# Revit family: QF_Franke_AC125CL_Foot05_en
name_source: partatom
category: Specialty Equipment
revit_build: Autodesk Revit 2018 (Build: 20170223_1515(x64)
units: mm (PartAtom-declared; Revit-internal decimal feet)

## family parameters
Always vertical = Yes
Cut with Voids When Loaded = No
OmniClass Number = 23.40.40.00
OmniClass Title = Food Service Equipment and Furnishings
Part Type = Normal
Room Calculation Point = No
Round Connector Dimension = Use Diameter
Shared = No
Work Plane-Based = No

## types (1)
- 110-240V 1L N PE data depending on system 10A - (all)
    Assembly Code = E1090320
    CE Approved = Yes
    Conn Conduit = Yes
    Cover front = QF_Black
    Cycle = 0 Hz
    Cycle Alternative = 0 Hz
    Depth Actual = 310 mm  [stored 1.01706 ft]
    ETL Approved = Yes
    Energy efficiency label = -
    Energy loss acc. to DIN 18873 = -
    Height Actual = 155 mm  [stored 0.50853 ft]
    Installed By = Franke technician or authorized Franke partner company
    Keynote = 11 46 23
    Length Actual = 125 mm  [stored 0.410105 ft]
    Manufacturer = Franke Kaffeemaschinen AG
    Max Overcurrent Protection = 10 A
    Model = AC125CL Foot05
    Noise emission = < 70 dB (A)
    Number of Nutral Conductors = 1
    Number of Poles = 1
    Number of Protective Conductors = 1
    Omniclass Number = 23.40.40.14.14.14
    Power consumption = 0 A
    Specification by Manufacturer = The add-on unit AC125CL is prepared for the integration of a customer own value- or money card system.
    URL = https://www.franke.com
    URL Critical Spares List = https://shop.franke.com
    URL Cutsheet = https://www.franke.com
    URL Manufacturer = https://www.franke.com
    Volts max. = 240 V
    Volts min. = 110 V
    Warranty Duration = 12 Mon.
    Watts max. = 0 W
    Watts min. = 0 W
    Weight = 2.00 kg

note: [stored X ft] marks values corroborated as IEEE doubles in the binary element streams (Revit-internal decimal feet)
